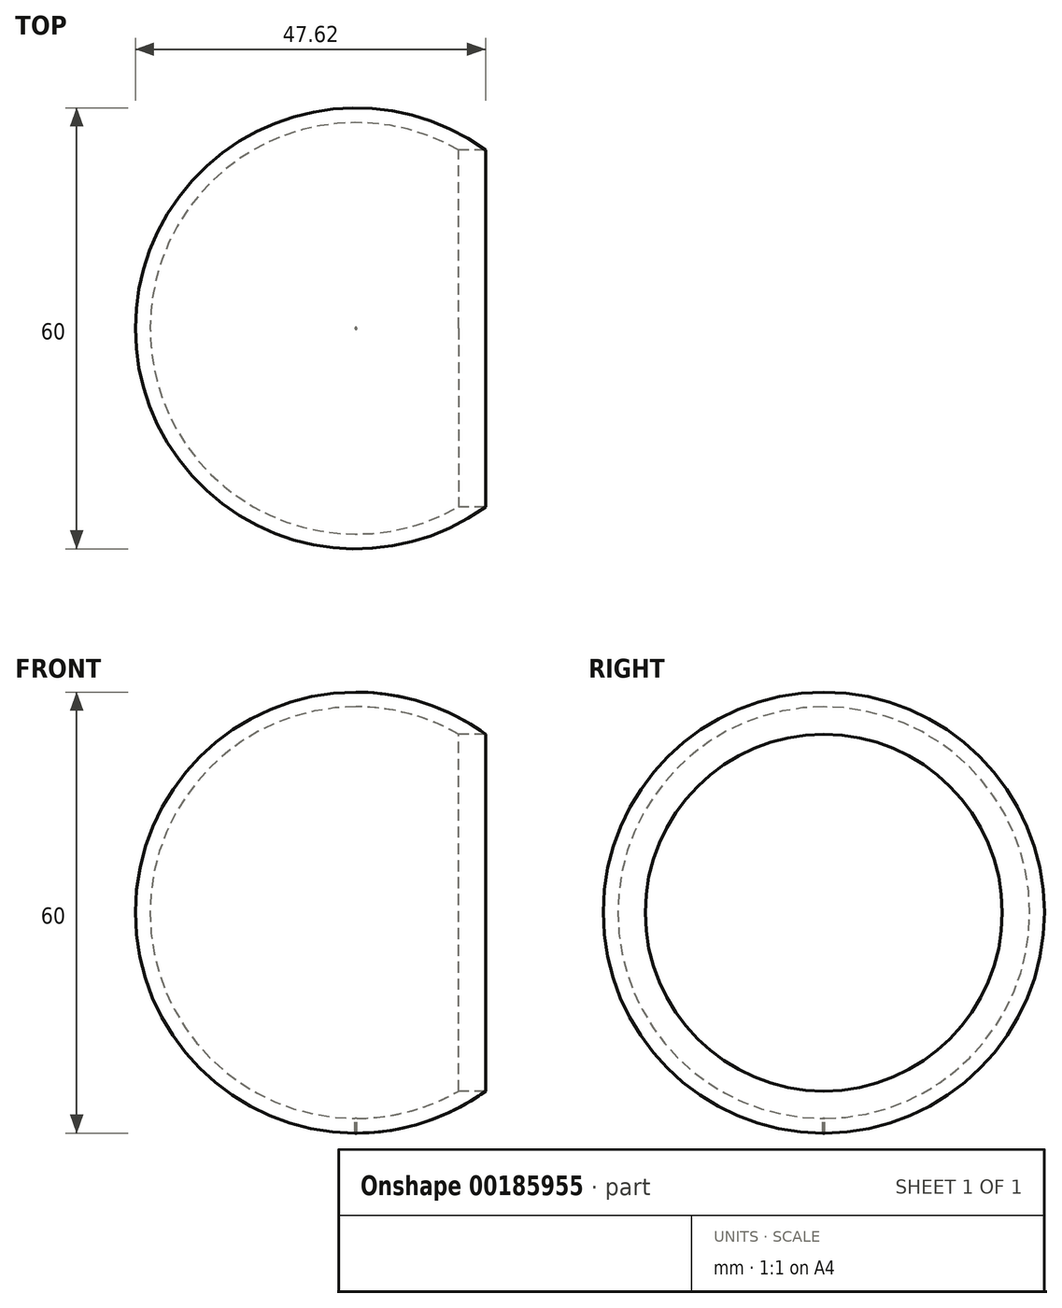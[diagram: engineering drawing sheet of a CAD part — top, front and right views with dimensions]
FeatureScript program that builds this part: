
annotation { "Feature Type Name" : "Feature", "Feature Type Description" : "" }
export const myFeature = defineFeature(function(context is Context, id is Id, definition is map)
    precondition{}
    {
        {
            var Q0;
            Q0=qCreatedBy(makeId("Front.planeOp"),FACE);
            var sketch = newSketch(context, id + "F0", { "sketchPlane" : qUnion([Q0])});
            skLineSegment(sketch, "E0", {"start": v(0, 44.72) * mm, "end": v(0, 36.63) * mm});
            skArc(sketch, "E1", {"start": v(0.12, -30) * mm, "mid": v(30, 0.06) * mm, "end": v(0, 30) * mm});
            skLineSegment(sketch, "E2", {"start": v(0, 30) * mm, "end": v(0, 28) * mm});
            skLineSegment(sketch, "E3", {"start": v(0.12, -30) * mm, "end": v(0.12, -28) * mm});
            skArc(sketch, "E4", {"start": v(0.12, -28) * mm, "mid": v(28, 0.06) * mm, "end": v(0, 28) * mm});
            skSolve(sketch);
        }
        {
            var Q0;
            Q0=makeQuery(id+"F0.imprint","IMPRINT",FACE,{"disambiguationData":[TD([[makeQuery(id+"F0.imprint","IMPRINT",EDGE,{"derivedFrom":sQuery(id+"F0.wireOp",EDGE,"PEyVn8QG-IJXN-QYcC-ioQH-3qW3VG6NlV5S")}),1.0]])]});
            var Q1;
            Q1=makeQuery(id+"F0.imprint","IMPRINT",FACE,{"disambiguationData":[TD([[makeQuery(id+"F0.imprint","IMPRINT",EDGE,{"derivedFrom":sQuery(id+"F0.wireOp",EDGE,"E1")}),1.0]])]});
            var Q2;
            Q2=sQuery(id+"F0.wireOp",EDGE,"E0");
            revolve(context, id + "F1", {"entities" : qUnion([Q0, Q1]), "axis" : qUnion([Q2]), "revolveType" : RevolveType.FULL});
        }
        {
            var Q0;
            Q0=qCreatedBy(makeId("Right.planeOp"),FACE);
            var sketch = newSketch(context, id + "F2", { "sketchPlane" : qUnion([Q0])});
            skCircle(sketch, "E5", {"center": v(0, 0) * mm, "radius": 24.28 * mm});
            skSolve(sketch);
        }
        {
            var Q0;
            Q0 = qSketchRegion(id + "F2", true);
            extrude(context, id + "F3", {"entities" : qUnion([Q0]), "operationType" : NewBodyOperationType.REMOVE, "depth" : 38.8 * mm});
        }
    });
